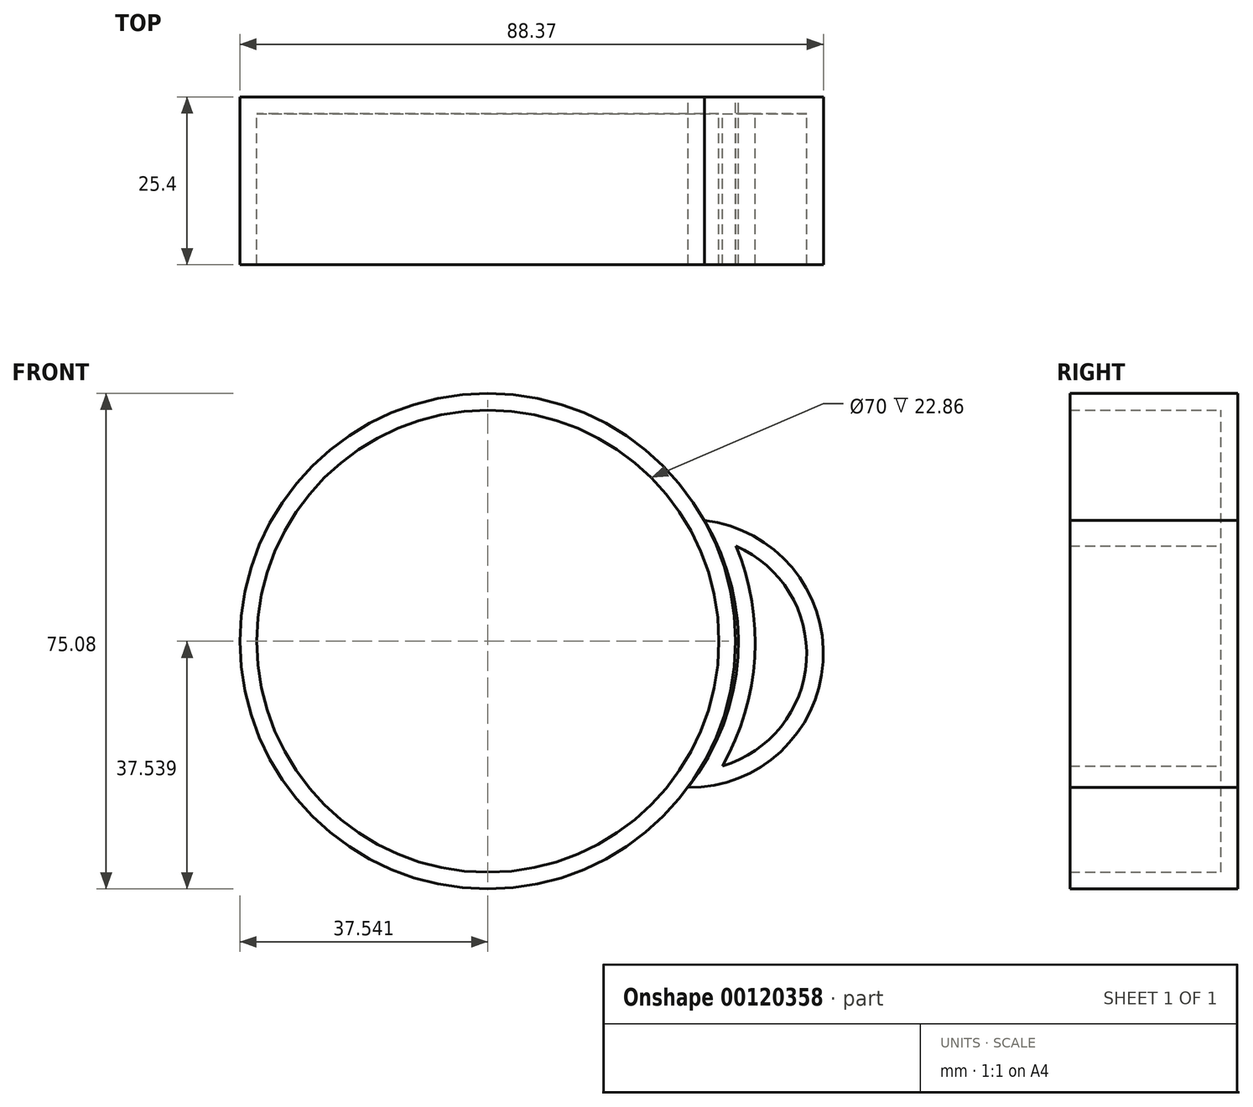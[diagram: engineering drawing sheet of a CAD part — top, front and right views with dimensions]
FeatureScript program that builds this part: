
annotation { "Feature Type Name" : "Feature", "Feature Type Description" : "" }
export const myFeature = defineFeature(function(context is Context, id is Id, definition is map)
    precondition{}
    {
        {
            var Q0;
            Q0=qCreatedBy(makeId("Front.planeOp"),FACE);
            var sketch = newSketch(context, id + "F0", { "sketchPlane" : qUnion([Q0])});
            skCircle(sketch, "E0", {"center": v(-22.82, 25.53) * mm, "radius": 37.54 * mm});
            skArc(sketch, "E1", {"start": v(7.49, 3.38) * mm, "mid": v(27.97, 22.4) * mm, "end": v(9.97, 43.8) * mm});
            skArc(sketch, "E2", {"start": v(7.49, 3.38) * mm, "mid": v(15.07, 23.2) * mm, "end": v(9.97, 43.8) * mm});
            skSolve(sketch);
        }
        {
            var Q0;
            Q0=makeQuery(id+"F0.imprint","IMPRINT",FACE,{"disambiguationData":[TD([[makeQuery(id+"F0.imprint","IMPRINT",EDGE,{"derivedFrom":sQuery(id+"F0.wireOp",EDGE,"E0")}),1.0]])]});
            var Q1;
            {var subQ0=sQuery(id+"F0.wireOp",EDGE,"E1");Q1=makeQuery(id+"F0.imprint","IMPRINT",FACE,{"disambiguationData":[TD([[makeQuery(id+"F0.imprint","IMPRINT",EDGE,{"derivedFrom":subQ0}),1.0]])]});}
            extrude(context, id + "F1", {"entities" : qUnion([Q0, Q1]), "depth" : 25.4 * mm});
        }
        {
            var Q0;
            Q0=makeQuery(id+"F1.opExtrude","CAP_FACE",FACE,{"disambiguationData":[OSD([sQuery(id+"F0.wireOp",EDGE,"E1"),sQuery(id+"F0.wireOp",EDGE,"E2")])],"isStart":false});
            var Q1;
            Q1=makeQuery(id+"F1.opExtrude","CAP_FACE",FACE,{"disambiguationData":[OSD([sQuery(id+"F0.wireOp",EDGE,"E0")])],"isStart":false});
            shell(context, id + "F2", {"entities" : qUnion([Q0, Q1]), "thickness" : 2.54 * mm});
        }
    });
